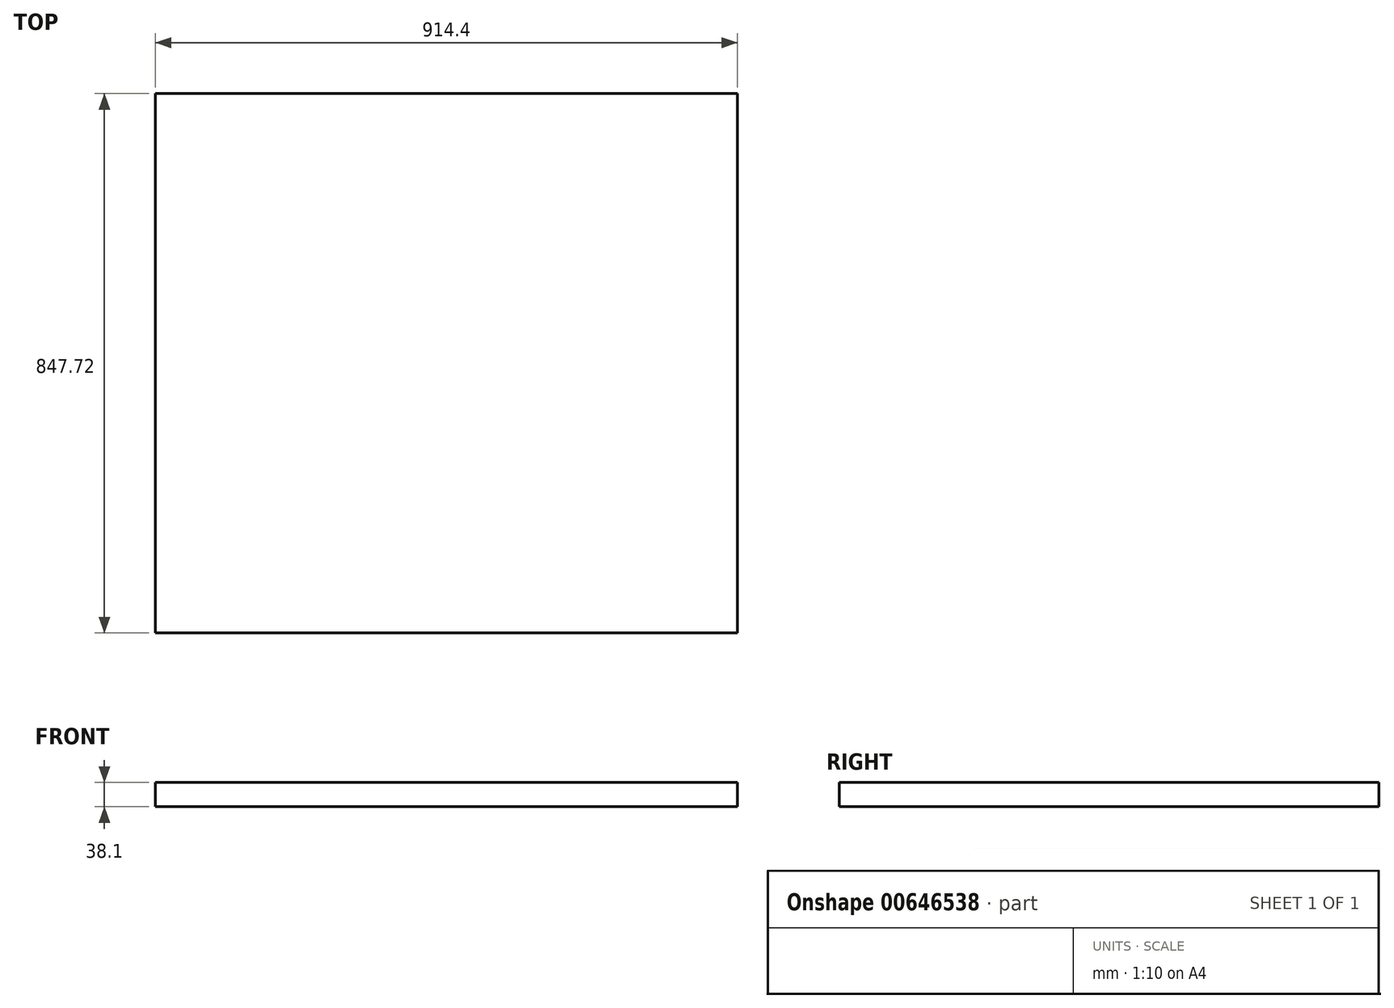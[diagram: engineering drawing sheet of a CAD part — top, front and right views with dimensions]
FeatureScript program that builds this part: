
annotation { "Feature Type Name" : "Feature", "Feature Type Description" : "" }
export const myFeature = defineFeature(function(context is Context, id is Id, definition is map)
    precondition{}
    {
        {
            var Q0;
            Q0=qCreatedBy(makeId("Top.planeOp"),FACE);
            var sketch = newSketch(context, id + "F0", { "sketchPlane" : qUnion([Q0])});
            skLineSegment(sketch, "E0.bottom", {"start": v(457.2, 423.86) * mm, "end": v(-457.2, 423.86) * mm});
            skLineSegment(sketch, "E0.top", {"start": v(457.2, -423.86) * mm, "end": v(-457.2, -423.86) * mm});
            skLineSegment(sketch, "E0.left", {"start": v(457.2, 423.86) * mm, "end": v(457.2, -423.86) * mm});
            skLineSegment(sketch, "E0.right", {"start": v(-457.2, 423.86) * mm, "end": v(-457.2, -423.86) * mm});
            skPoint(sketch, "E0.middle", {"position": v(0, 0) * mm});
            skSolve(sketch);
        }
        {
            var Q0;
            Q0=makeQuery(id+"F0.imprint","IMPRINT",FACE,{"disambiguationData":[TD([[makeQuery(id+"F0.imprint","IMPRINT",EDGE,{"derivedFrom":sQuery(id+"F0.wireOp",EDGE,"E0.bottom")}),1.0]])]});
            extrude(context, id + "F1", {"entities" : qUnion([Q0]), "depth" : 38.1 * mm, "offsetDistance" : 25.4 * mm});
        }
    });
